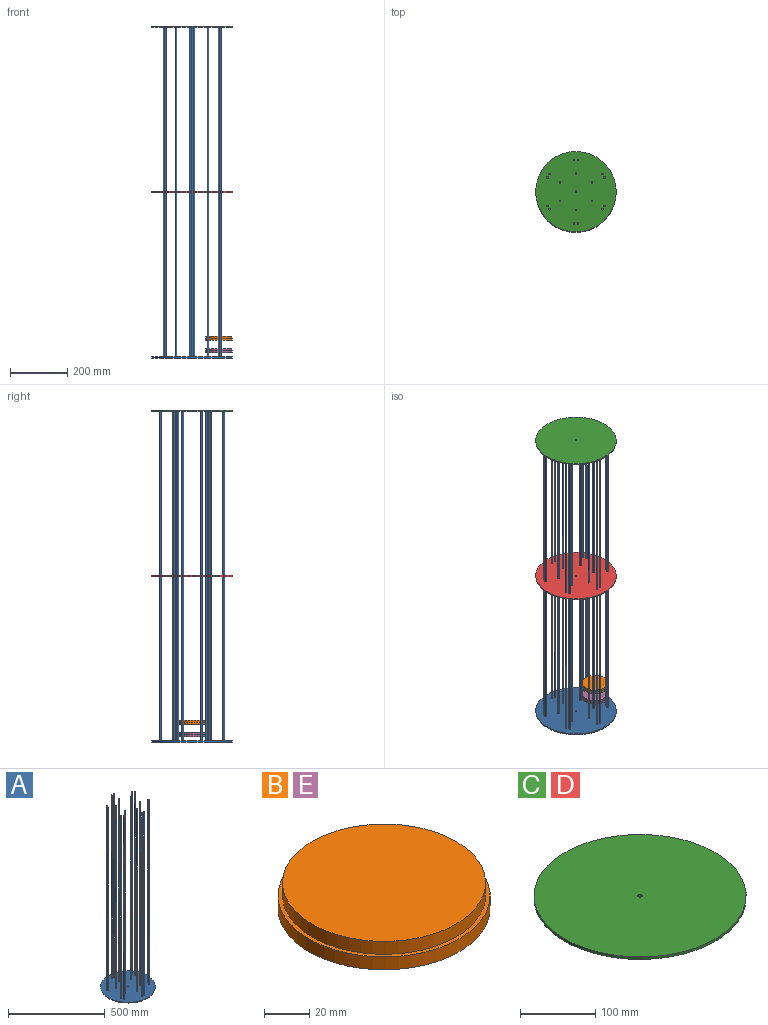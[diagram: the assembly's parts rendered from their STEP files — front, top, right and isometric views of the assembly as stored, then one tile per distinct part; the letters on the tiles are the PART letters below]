
ASSEMBLY  parts=5 mates=4
PART A: 41 faces, bbox 282x282x1160 mm
  f0: cylinder r=3mm len=6mm, axis (0,0,-1), area 75.4mm2, adj f3,f4
  f1: cylinder r=141mm len=282mm, axis (0,0,-1), area 3543.7mm2, adj f3,f4
  f2: cylinder r=3mm len=6mm, axis (0,0,-1), area 75.4mm2, adj f3,f4
  f3: plane 282x282mm, normal (0,0,1), area 61892.5mm2, adj f0,f1,f2,f5,f7,f9,f11,f13
  f4: plane 282x282mm, normal (0,0,-1), area 62401.5mm2, adj f0,f1,f2
  f5: cylinder r=3mm len=1156mm, axis (0,0,-1), area 21790.1mm2, adj f3,f6
  f6: plane 6x6mm, normal (0,0,1), area 28.3mm2, adj f5
  f7: cylinder r=3mm len=1156mm, axis (0,0,-1), area 21790.1mm2, adj f3,f8
  f8: plane 6x6mm, normal (0,0,1), area 28.3mm2, adj f7
  f9: cylinder r=3mm len=1156mm, axis (0,0,-1), area 21790.1mm2, adj f3,f10
  f10: plane 6x6mm, normal (0,0,1), area 28.3mm2, adj f9
  f11: cylinder r=3mm len=1156mm, axis (0,0,-1), area 21790.1mm2, adj f3,f12
  f12: plane 6x6mm, normal (0,0,1), area 28.3mm2, adj f11
  f13: cylinder r=3mm len=1156mm, axis (0,0,-1), area 21790.1mm2, adj f3,f14
  f14: plane 6x6mm, normal (0,0,1), area 28.3mm2, adj f13
  f15: cylinder r=3mm len=1156mm, axis (0,0,-1), area 21790.1mm2, adj f3,f16
  f16: plane 6x6mm, normal (0,0,1), area 28.3mm2, adj f15
  f17: cylinder r=3mm len=1156mm, axis (0,0,-1), area 21790.1mm2, adj f3,f18
  f18: plane 6x6mm, normal (0,0,1), area 28.3mm2, adj f17
  f19: cylinder r=3mm len=1156mm, axis (0,0,-1), area 21790.1mm2, adj f3,f20
  f20: plane 6x6mm, normal (0,0,1), area 28.3mm2, adj f19
  f21: cylinder r=3mm len=1156mm, axis (0,0,-1), area 21790.1mm2, adj f3,f22
  f22: plane 6x6mm, normal (0,0,1), area 28.3mm2, adj f21
  f23: cylinder r=3mm len=1156mm, axis (0,0,-1), area 21790.1mm2, adj f3,f24
  f24: plane 6x6mm, normal (0,0,1), area 28.3mm2, adj f23
  f25: cylinder r=3mm len=1156mm, axis (0,0,-1), area 21790.1mm2, adj f3,f26
  f26: plane 6x6mm, normal (0,0,1), area 28.3mm2, adj f25
  f27: cylinder r=3mm len=1156mm, axis (0,0,-1), area 21790.1mm2, adj f3,f28
  f28: plane 6x6mm, normal (0,0,1), area 28.3mm2, adj f27
  f29: cylinder r=3mm len=1156mm, axis (0,0,-1), area 21790.1mm2, adj f3,f30
  f30: plane 6x6mm, normal (0,0,1), area 28.3mm2, adj f29
  f31: cylinder r=3mm len=1156mm, axis (0,0,-1), area 21790.1mm2, adj f3,f32
  f32: plane 6x6mm, normal (0,0,1), area 28.3mm2, adj f31
  f33: cylinder r=3mm len=1156mm, axis (0,0,-1), area 21790.1mm2, adj f3,f34
  f34: plane 6x6mm, normal (0,0,1), area 28.3mm2, adj f33
  f35: cylinder r=3mm len=1156mm, axis (0,0,-1), area 21790.1mm2, adj f3,f36
  f36: plane 6x6mm, normal (0,0,1), area 28.3mm2, adj f35
  f37: cylinder r=3mm len=1156mm, axis (0,0,-1), area 21790.1mm2, adj f3,f38
  f38: plane 6x6mm, normal (0,0,1), area 28.3mm2, adj f37
  f39: cylinder r=3mm len=1156mm, axis (0,0,-1), area 21790.1mm2, adj f3,f40
  f40: plane 6x6mm, normal (0,0,1), area 28.3mm2, adj f39
PART B: 5 faces, bbox 94x94x14 mm
  f0: cylinder r=47mm len=94mm, axis (0,0,-1), area 2067.2mm2, adj f1,f2
  f1: plane 94x94mm, normal (0,0,1), area 578.1mm2, adj f0,f3
  f2: plane 94x94mm, normal (0,0,-1), area 6939.8mm2, adj f0
  f3: cylinder r=45mm len=90mm, axis (0,0,-1), area 1979.2mm2, adj f1,f4
  f4: plane 90x90mm, normal (0,0,1), area 6361.7mm2, adj f3
PART C: 4 faces, bbox 282x282x4 mm
  f0: cylinder r=3mm len=6mm, axis (0,0,-1), area 75.4mm2, adj f2,f3
  f1: cylinder r=141mm len=282mm, axis (0,0,-1), area 3543.7mm2, adj f2,f3
  f2: plane 282x282mm, normal (0,0,1), area 62429.7mm2, adj f0,f1
  f3: plane 282x282mm, normal (0,0,-1), area 62429.7mm2, adj f0,f1
PART D: same geometry as C
PART E: same geometry as B
PLACE A t=(-1333.62,2038.24,-2703.85)mm
PLACE B rot(axis=(0,0,-1),0deg) t=(-1239.62,2038.24,-2641.23)mm
PLACE C t=(-1713.28,2038.24,-1543.85)mm
PLACE D t=(-1713.28,2038.24,-2123.85)mm
PLACE E rot(axis=(0,0,1),0deg) t=(-1239.62,2038.24,-2685.85)mm
MATE fastened D.f1 <-> A.f2  axis (0,0,1) through (-1333.62,2038.24,-2119.85)mm
MATE cylindrical B.f3 <-> E.f3  axis (0,0,1) through (-1239.62,2038.24,-2627.23)mm
MATE fastened A.f2 <-> C.f1  axis (0,0,1) through (-1333.62,2038.24,-2699.85)mm
MATE cylindrical B.f3 <-> A.f0  axis (0,0,1) through (-1239.62,2038.24,-2627.23)mm
